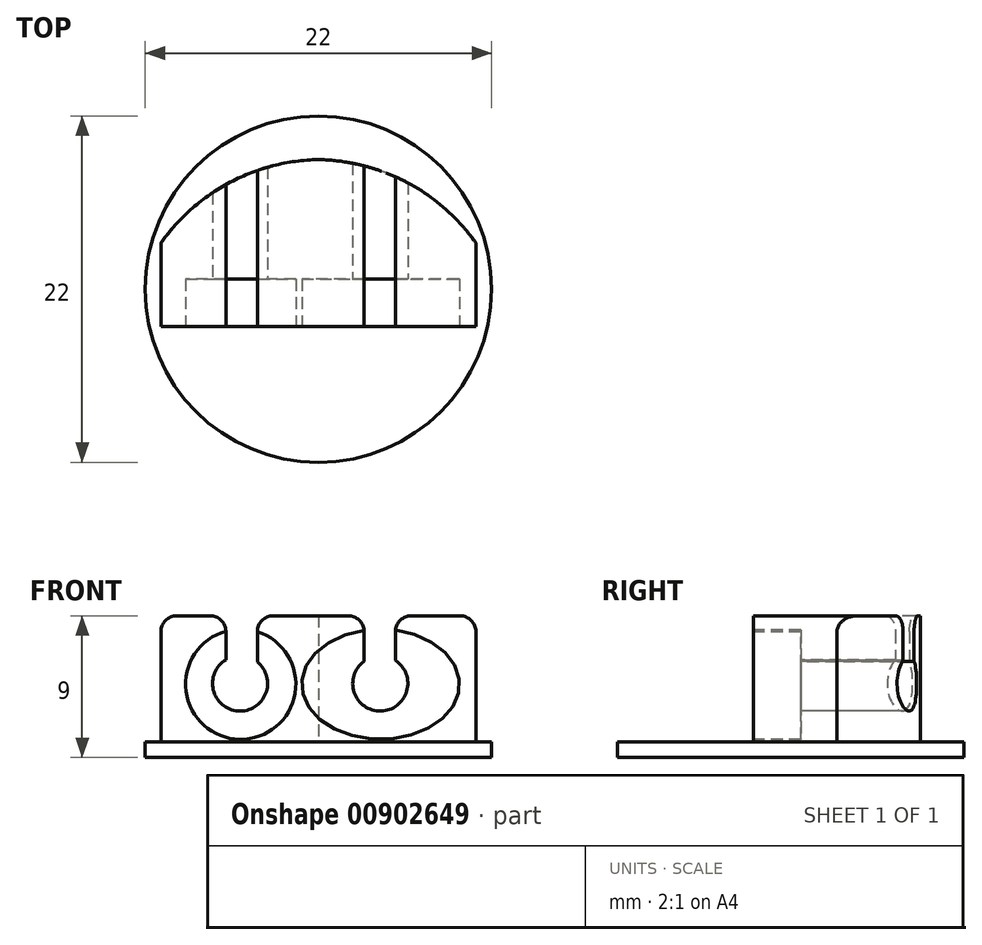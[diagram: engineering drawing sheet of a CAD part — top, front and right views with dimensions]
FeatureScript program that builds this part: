
annotation { "Feature Type Name" : "Feature", "Feature Type Description" : "" }
export const myFeature = defineFeature(function(context is Context, id is Id, definition is map)
    precondition{}
    {
        {
            var Q0;
            Q0=qCreatedBy(makeId("Top.planeOp"),FACE);
            var sketch = newSketch(context, id + "F0", { "sketchPlane" : qUnion([Q0])});
            skCircle(sketch, "E0", {"center": v(0, 0) * mm, "radius": 11 * mm});
            skSolve(sketch);
        }
        {
            var Q0;
            Q0=makeQuery(id+"F0.imprint","IMPRINT",FACE,{"disambiguationData":[TD([[makeQuery(id+"F0.imprint","IMPRINT",EDGE,{"derivedFrom":sQuery(id+"F0.wireOp",EDGE,"E0")}),1.0]])]});
            extrude(context, id + "F1", {"entities" : qUnion([Q0]), "depth" : 1 * mm, "offsetDistance" : 25 * mm});
        }
        {
            var Q0;
            Q0=makeQuery(id+"F1.opExtrude","CAP_FACE",FACE,{"disambiguationData":[OSD([sQuery(id+"F0.wireOp",EDGE,"E0")])],"isStart":false});
            var sketch = newSketch(context, id + "F2", { "sketchPlane" : qUnion([Q0])});
            skLineSegment(sketch, "E1.bottom", {"start": v(10, -2.36) * mm, "end": v(-10, -2.36) * mm});
            skLineSegment(sketch, "E1.left", {"start": v(10, -2.36) * mm, "end": v(10, 2.93) * mm});
            skLineSegment(sketch, "E1.right", {"start": v(-10, -2.36) * mm, "end": v(-10, 2.93) * mm});
            skPoint(sketch, "E1.middle", {"position": v(0, 2.93) * mm});
            skArc(sketch, "E2", {"start": v(0, 8.23) * mm, "mid": v(-5.63, 6.77) * mm, "end": v(-10, 2.93) * mm});
            skArc(sketch, "E3.MirrorCS", {"start": v(0, 8.23) * mm, "mid": v(5.63, 6.77) * mm, "end": v(10, 2.93) * mm});
            skPoint(sketch, "E4.orphan", {"position": v(-10, 8.23) * mm});
            skPoint(sketch, "E5.orphan", {"position": v(10, 8.23) * mm});
            skSolve(sketch);
        }
        {
            var Q0;
            Q0=makeQuery(id+"F2.imprint","IMPRINT",FACE,{"disambiguationData":[TD([[makeQuery(id+"F2.imprint","IMPRINT",EDGE,{"derivedFrom":sQuery(id+"F2.wireOp",EDGE,"E1.bottom")}),-1.0]])]});
            extrude(context, id + "F3", {"entities" : qUnion([Q0]), "operationType" : NewBodyOperationType.ADD, "depth" : 8 * mm, "offsetDistance" : 25 * mm});
        }
        {
            var Q0;
            Q0=makeQuery(id+"F3.opExtrude","SWEPT_FACE",FACE,{"disambiguationData":[OSD([sQuery(id+"F2.wireOp",EDGE,"E1.bottom")])]});
            var sketch = newSketch(context, id + "F4", { "sketchPlane" : qUnion([Q0])});
            skCircle(sketch, "E6", {"center": v(-4.93, 4.65) * mm, "radius": 3.5 * mm});
            skEllipse(sketch, "E7", {"center": v(3.95, 4.65) * mm, "majorRadius": 5 * mm, "minorRadius": 3.5 * mm, "majorAxis": v(1, 0)});
            skSolve(sketch);
        }
        {
            var Q0;
            Q0=makeQuery(id+"F4.imprint","IMPRINT",FACE,{"disambiguationData":[TD([[makeQuery(id+"F4.imprint","IMPRINT",EDGE,{"derivedFrom":sQuery(id+"F4.wireOp",EDGE,"E7")}),1.0]])]});
            var Q1;
            Q1=makeQuery(id+"F4.imprint","IMPRINT",FACE,{"disambiguationData":[TD([[makeQuery(id+"F4.imprint","IMPRINT",EDGE,{"derivedFrom":sQuery(id+"F4.wireOp",EDGE,"E6")}),1.0]])]});
            extrude(context, id + "F5", {"entities" : qUnion([Q0, Q1]), "operationType" : NewBodyOperationType.REMOVE, "oppositeDirection" : true, "depth" : 3 * mm, "offsetDistance" : 25 * mm});
        }
        {
            var Q0;
            Q0=makeQuery(id+"F4.imprint","IMPRINT",FACE,{"disambiguationData":[TD([[makeQuery(id+"F4.imprint","IMPRINT",EDGE,{"derivedFrom":sQuery(id+"F4.wireOp",EDGE,"E6")}),1.0]])]});
            var sketch = newSketch(context, id + "F6", { "sketchPlane" : qUnion([Q0])});
            skCircle(sketch, "E8", {"center": v(-4.98, 4.7) * mm, "radius": 1.75 * mm});
            skCircle(sketch, "E9", {"center": v(3.93, 4.7) * mm, "radius": 1.75 * mm});
            skSolve(sketch);
        }
        {
            var Q0;
            Q0 = qSketchRegion(id + "F6", true);
            extrude(context, id + "F7", {"entities" : qUnion([Q0]), "operationType" : NewBodyOperationType.REMOVE, "oppositeDirection" : true, "depth" : 25 * mm, "offsetDistance" : 25 * mm});
        }
        {
            var Q0;
            Q0=makeQuery(id+"F4.imprint","IMPRINT",FACE,{"disambiguationData":[TD([[makeQuery(id+"F4.imprint","IMPRINT",EDGE,{"derivedFrom":sQuery(id+"F4.wireOp",EDGE,"E6")}),-1.0]])]});
            var sketch = newSketch(context, id + "F8", { "sketchPlane" : qUnion([Q0])});
            skLineSegment(sketch, "E10", {"start": v(-5.01, 4.75) * mm, "end": v(-5.01, 14.24) * mm, "construction": true});
            skLineSegment(sketch, "E11", {"start": v(3.92, 4.9) * mm, "end": v(3.92, 14.44) * mm, "construction": true});
            skLineSegment(sketch, "E12.bottom", {"start": v(-5.88, 10.36) * mm, "end": v(-3.88, 10.36) * mm});
            skLineSegment(sketch, "E12.top", {"start": v(-5.88, 5.36) * mm, "end": v(-3.88, 5.36) * mm});
            skLineSegment(sketch, "E12.left", {"start": v(-5.88, 10.36) * mm, "end": v(-5.88, 5.36) * mm});
            skLineSegment(sketch, "E12.right", {"start": v(-3.88, 10.36) * mm, "end": v(-3.88, 5.36) * mm});
            skLineSegment(sketch, "E13.bottom", {"start": v(2.9, 9.86) * mm, "end": v(4.9, 9.86) * mm});
            skLineSegment(sketch, "E13.top", {"start": v(2.9, 4.86) * mm, "end": v(4.9, 4.86) * mm});
            skLineSegment(sketch, "E13.left", {"start": v(2.9, 9.86) * mm, "end": v(2.9, 4.86) * mm});
            skLineSegment(sketch, "E13.right", {"start": v(4.9, 9.86) * mm, "end": v(4.9, 4.86) * mm});
            skSolve(sketch);
        }
        {
            var Q0;
            {var subQ0=sQuery(id+"F8.wireOp",EDGE,"E12.bottom");Q0=makeQuery(id+"F8.imprint","IMPRINT",FACE,{"disambiguationData":[TD([[makeQuery(id+"F8.imprint","IMPRINT",EDGE,{"derivedFrom":subQ0}),-1.0]])]});}
            var Q1;
            {var subQ0=sQuery(id+"F8.wireOp",EDGE,"E12.left");var subQ1=makeQuery(id+"F4.imprint","IMPRINT",EDGE,{"derivedFrom":makeQuery(id+"F3.opExtrude","CAP_EDGE",EDGE,{"disambiguationData":[OSD([sQuery(id+"F2.wireOp",EDGE,"E1.bottom")])],"isStart":false})});var subQ2=makeQuery(id+"F8.imprint","INTERSECT",VERTEX,{"derivedFrom":[subQ1,subQ0]});Q1=makeQuery(id+"F8.imprint","IMPRINT",FACE,{"disambiguationData":[TD([[makeQuery(id+"F8.imprint","IMPRINT",EDGE,{"disambiguationData":[TD([[subQ2,-1.0]])],"derivedFrom":subQ0}),1.0]])]});}
            var Q2;
            {var subQ0=sQuery(id+"F8.wireOp",EDGE,"E12.top");Q2=makeQuery(id+"F8.imprint","IMPRINT",FACE,{"disambiguationData":[TD([[makeQuery(id+"F8.imprint","IMPRINT",EDGE,{"derivedFrom":subQ0}),1.0]])]});}
            var Q3;
            {var subQ0=sQuery(id+"F8.wireOp",EDGE,"E13.top");Q3=makeQuery(id+"F8.imprint","IMPRINT",FACE,{"disambiguationData":[TD([[makeQuery(id+"F8.imprint","IMPRINT",EDGE,{"derivedFrom":subQ0}),1.0]])]});}
            var Q4;
            {var subQ0=sQuery(id+"F8.wireOp",EDGE,"E13.left");var subQ1=makeQuery(id+"F4.imprint","IMPRINT",EDGE,{"derivedFrom":makeQuery(id+"F3.opExtrude","CAP_EDGE",EDGE,{"disambiguationData":[OSD([sQuery(id+"F2.wireOp",EDGE,"E1.bottom")])],"isStart":false})});var subQ2=makeQuery(id+"F8.imprint","INTERSECT",VERTEX,{"derivedFrom":[subQ1,subQ0]});Q4=makeQuery(id+"F8.imprint","IMPRINT",FACE,{"disambiguationData":[TD([[makeQuery(id+"F8.imprint","IMPRINT",EDGE,{"disambiguationData":[TD([[subQ2,-1.0]])],"derivedFrom":subQ0}),1.0]])]});}
            var Q5;
            {var subQ0=sQuery(id+"F8.wireOp",EDGE,"E13.bottom");Q5=makeQuery(id+"F8.imprint","IMPRINT",FACE,{"disambiguationData":[TD([[makeQuery(id+"F8.imprint","IMPRINT",EDGE,{"derivedFrom":subQ0}),-1.0]])]});}
            extrude(context, id + "F9", {"entities" : qUnion([Q0, Q1, Q2, Q3, Q4, Q5]), "operationType" : NewBodyOperationType.REMOVE, "oppositeDirection" : true, "depth" : 25 * mm, "offsetDistance" : 25 * mm});
        }
        {
            var Q0;
            Q0=makeQuery(id+"F3.opExtrude","CAP_EDGE",EDGE,{"disambiguationData":[OSD([sQuery(id+"F2.wireOp",EDGE,"E1.right")])],"isStart":false});
            var Q1;
            Q1=makeQuery(id+"F9.boolean.opBoolean","INTERSECT",EDGE,{"derivedFrom":[makeQuery(id+"F3.opExtrude","CAP_FACE",FACE,{"disambiguationData":[OSD([sQuery(id+"F2.wireOp",EDGE,"E1.bottom"),sQuery(id+"F2.wireOp",EDGE,"E1.left"),sQuery(id+"F2.wireOp",EDGE,"E1.right"),sQuery(id+"F2.wireOp",EDGE,"E2"),sQuery(id+"F2.wireOp",EDGE,"E3.MirrorCS")])],"isStart":false}),makeQuery(id+"F9.opExtrude","SWEPT_FACE",FACE,{"disambiguationData":[OSD([sQuery(id+"F8.wireOp",EDGE,"E12.left")])]})]});
            var Q2;
            Q2=makeQuery(id+"F9.boolean.opBoolean","INTERSECT",EDGE,{"derivedFrom":[makeQuery(id+"F3.opExtrude","CAP_FACE",FACE,{"disambiguationData":[OSD([sQuery(id+"F2.wireOp",EDGE,"E1.bottom"),sQuery(id+"F2.wireOp",EDGE,"E1.left"),sQuery(id+"F2.wireOp",EDGE,"E1.right"),sQuery(id+"F2.wireOp",EDGE,"E2"),sQuery(id+"F2.wireOp",EDGE,"E3.MirrorCS")])],"isStart":false}),makeQuery(id+"F9.opExtrude","SWEPT_FACE",FACE,{"disambiguationData":[OSD([sQuery(id+"F8.wireOp",EDGE,"E12.right")])]})]});
            var Q3;
            Q3=makeQuery(id+"F9.boolean.opBoolean","INTERSECT",EDGE,{"derivedFrom":[makeQuery(id+"F3.opExtrude","CAP_FACE",FACE,{"disambiguationData":[OSD([sQuery(id+"F2.wireOp",EDGE,"E1.bottom"),sQuery(id+"F2.wireOp",EDGE,"E1.left"),sQuery(id+"F2.wireOp",EDGE,"E1.right"),sQuery(id+"F2.wireOp",EDGE,"E2"),sQuery(id+"F2.wireOp",EDGE,"E3.MirrorCS")])],"isStart":false}),makeQuery(id+"F9.opExtrude","SWEPT_FACE",FACE,{"disambiguationData":[OSD([sQuery(id+"F8.wireOp",EDGE,"E13.left")])]})]});
            var Q4;
            Q4=makeQuery(id+"F9.boolean.opBoolean","INTERSECT",EDGE,{"derivedFrom":[makeQuery(id+"F3.opExtrude","CAP_FACE",FACE,{"disambiguationData":[OSD([sQuery(id+"F2.wireOp",EDGE,"E1.bottom"),sQuery(id+"F2.wireOp",EDGE,"E1.left"),sQuery(id+"F2.wireOp",EDGE,"E1.right"),sQuery(id+"F2.wireOp",EDGE,"E2"),sQuery(id+"F2.wireOp",EDGE,"E3.MirrorCS")])],"isStart":false}),makeQuery(id+"F9.opExtrude","SWEPT_FACE",FACE,{"disambiguationData":[OSD([sQuery(id+"F8.wireOp",EDGE,"E13.right")])]})]});
            var Q5;
            Q5=makeQuery(id+"F3.opExtrude","CAP_EDGE",EDGE,{"disambiguationData":[OSD([sQuery(id+"F2.wireOp",EDGE,"E1.left")])],"isStart":false});
            fillet(context, id + "F10", {"entities" : qUnion([Q0, Q1, Q2, Q3, Q4, Q5]), "radius" : 1 * mm, "tangentPropagation" : true, "allowEdgeOverflow" : false});
        }
    });
